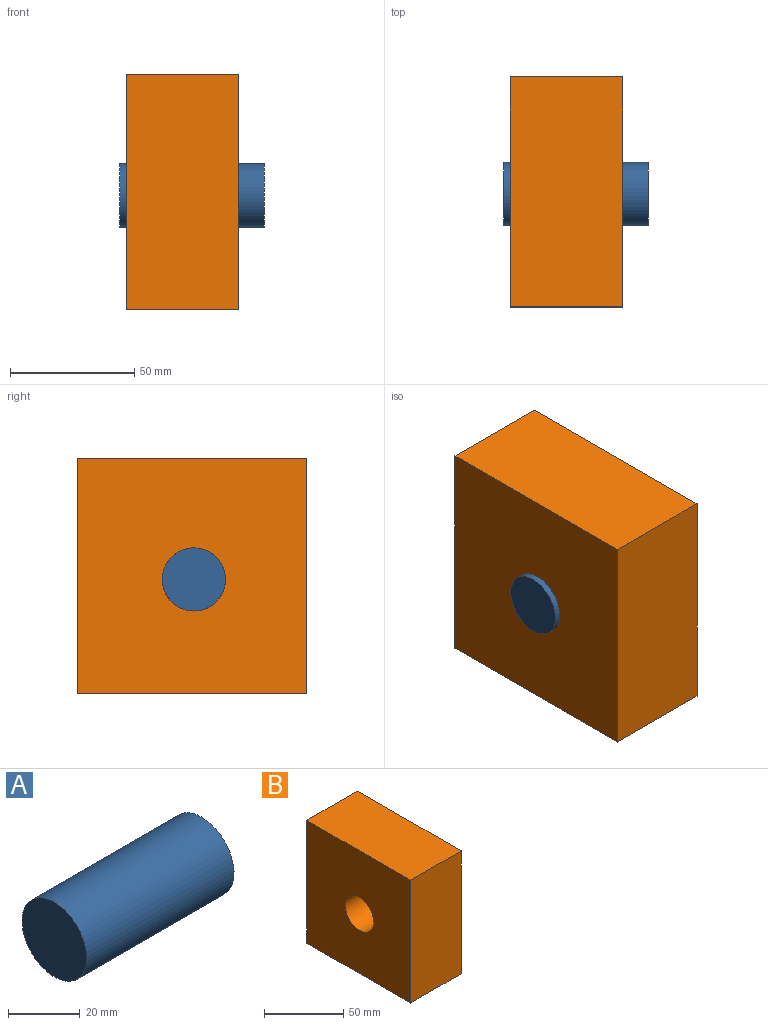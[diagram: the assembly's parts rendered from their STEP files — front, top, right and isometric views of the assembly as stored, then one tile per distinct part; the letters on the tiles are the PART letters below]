
ASSEMBLY  parts=2 mates=1
PART A: 3 faces, bbox 57.9x25.4x25.4 mm
  f0: cylinder r=12.7mm len=57.91mm, axis (-1,0,0), area 4621.2mm2, adj f1,f2
  f1: plane 25.4x25.4mm, normal (1,0,0), area 506.7mm2, adj f0
  f2: plane 25.4x25.4mm, normal (-1,0,0), area 506.7mm2, adj f0
PART B: 7 faces, bbox 45.2x92.4x94.7 mm
  f0: plane 92.42x45.21mm, normal (0,0,1), area 4178.3mm2, adj f1,f3,f4,f5
  f1: plane 94.7x45.21mm, normal (0,-1,0), area 4281.4mm2, adj f0,f2,f4,f5
  f2: plane 92.42x45.21mm, normal (0,0,-1), area 4178.3mm2, adj f1,f3,f4,f5
  f3: plane 94.7x45.21mm, normal (0,1,0), area 4281.4mm2, adj f0,f2,f4,f5
  f4: plane 94.7x92.42mm, normal (1,0,0), area 8244.7mm2, adj f0,f1,f2,f3,f6
  f5: plane 94.7x92.42mm, normal (-1,0,0), area 8244.7mm2, adj f0,f1,f2,f3,f6
  f6: cylinder r=12.7mm len=45.21mm, axis (-1,0,0), area 3607.8mm2, adj f4,f5
PLACE A t=(-48.88,-34.47,-13.02)mm
PLACE B t=(-46.31,-34.47,-13.02)mm
MATE cylindrical A.f0 <-> B.f6  axis (-1,0,0) through (-19.93,-34.47,-13.02)mm
